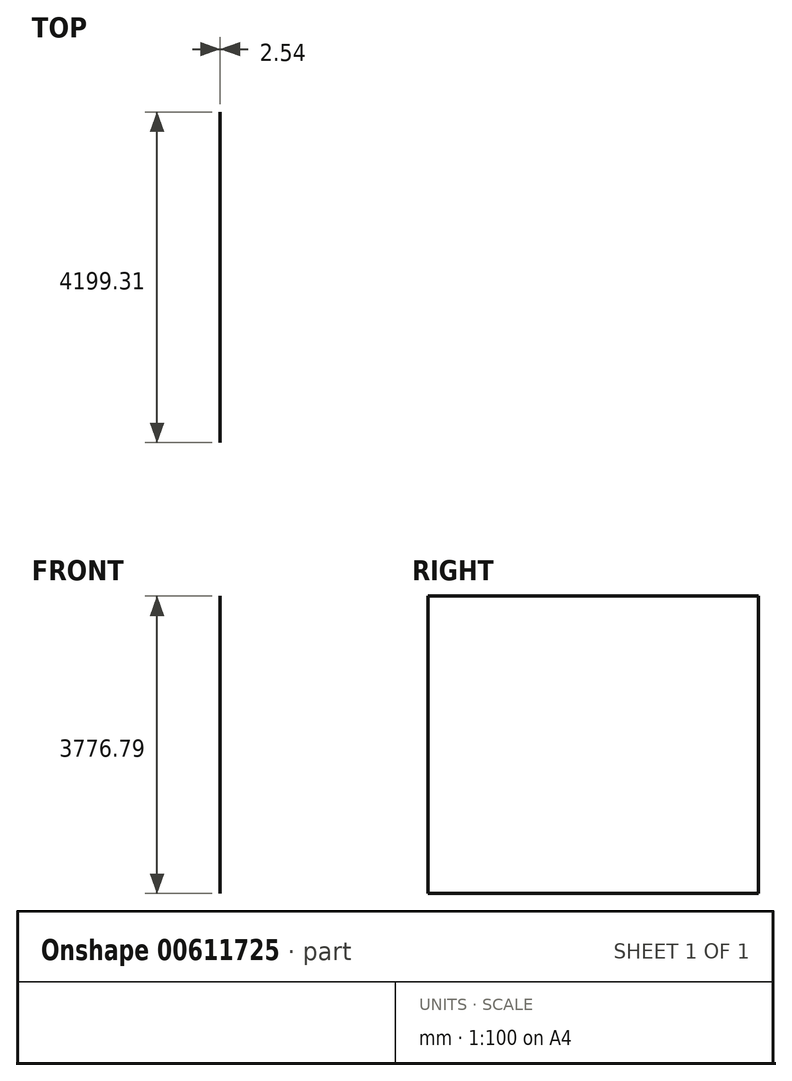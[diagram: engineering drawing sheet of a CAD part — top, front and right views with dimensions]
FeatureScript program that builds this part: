
annotation { "Feature Type Name" : "Feature", "Feature Type Description" : "" }
export const myFeature = defineFeature(function(context is Context, id is Id, definition is map)
    precondition{}
    {
        {
            var Q0;
            Q0=qCreatedBy(makeId("Right.planeOp"),FACE);
            var sketch = newSketch(context, id + "F0", { "sketchPlane" : qUnion([Q0])});
            skLineSegment(sketch, "E0.bottom", {"start": v(0, 0) * mm, "end": v(-4199.3, 0) * mm});
            skLineSegment(sketch, "E0.top", {"start": v(0, -3776.79) * mm, "end": v(-4199.3, -3776.79) * mm});
            skLineSegment(sketch, "E0.left", {"start": v(0, 0) * mm, "end": v(0, -3776.79) * mm});
            skLineSegment(sketch, "E0.right", {"start": v(-4199.3, 0) * mm, "end": v(-4199.3, -3776.79) * mm});
            skSolve(sketch);
        }
        {
            var Q0;
            Q0=makeQuery(id+"F0.imprint","IMPRINT",FACE,{"disambiguationData":[TD([[makeQuery(id+"F0.imprint","IMPRINT",EDGE,{"derivedFrom":sQuery(id+"F0.wireOp",EDGE,"E0.bottom")}),1.0]])]});
            extrude(context, id + "F1", {"entities" : qUnion([Q0]), "depth" : 2.54 * mm, "offsetDistance" : 25.4 * mm});
        }
    });
